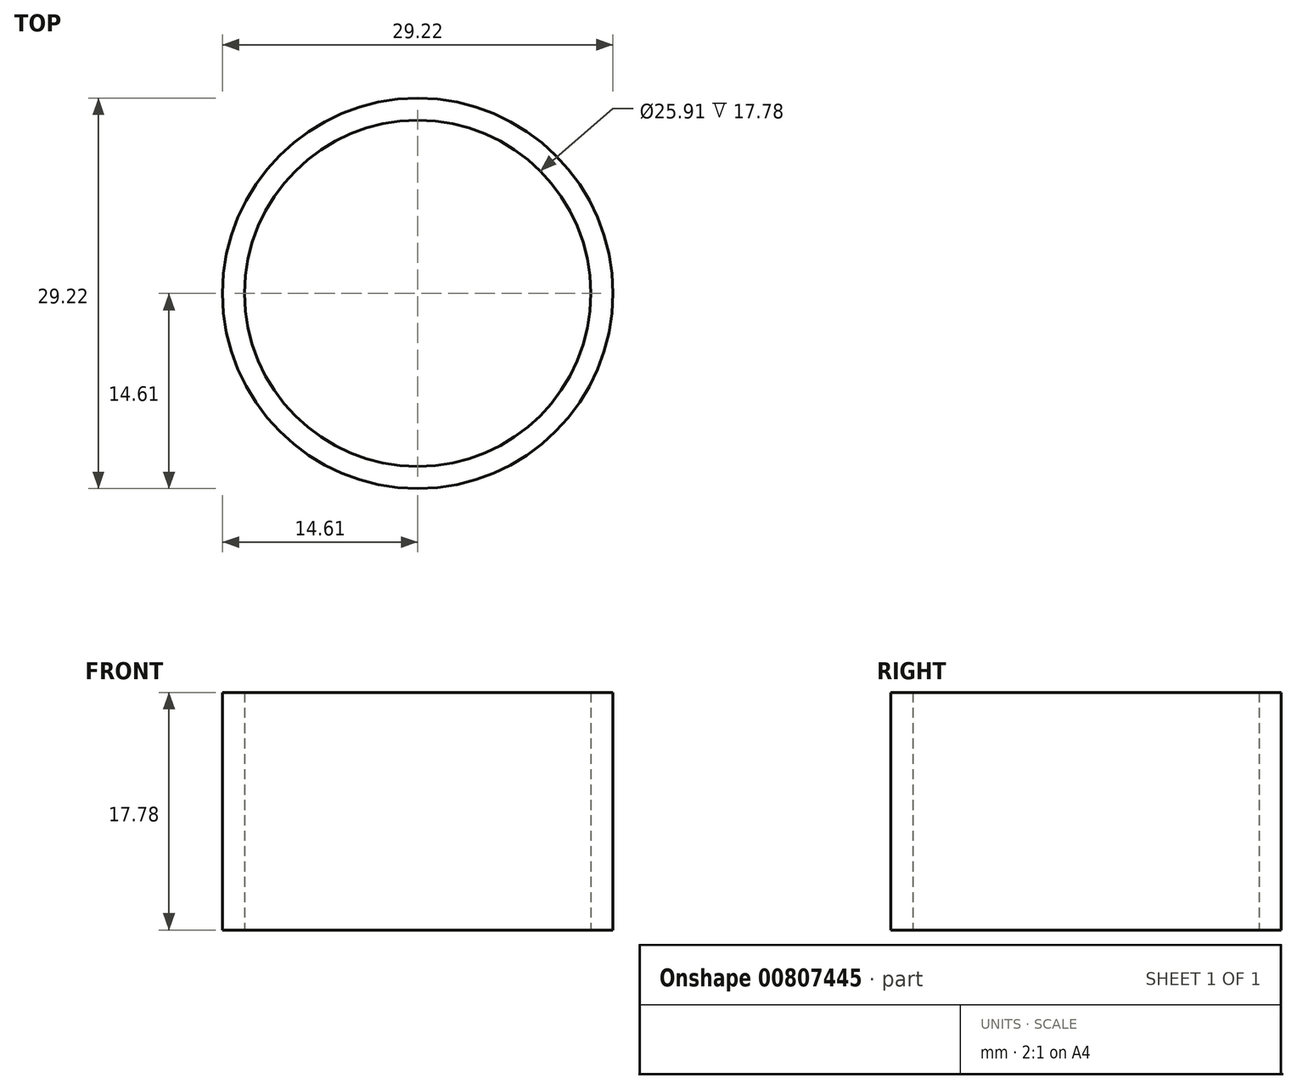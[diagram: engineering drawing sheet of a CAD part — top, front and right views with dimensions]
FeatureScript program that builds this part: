
annotation { "Feature Type Name" : "Feature", "Feature Type Description" : "" }
export const myFeature = defineFeature(function(context is Context, id is Id, definition is map)
    precondition{}
    {
        {
            var Q0;
            Q0=qCreatedBy(makeId("Top.planeOp"),FACE);
            var sketch = newSketch(context, id + "F0", { "sketchPlane" : qUnion([Q0])});
            skCircle(sketch, "E0", {"center": v(0, 0) * mm, "radius": 14.6 * mm});
            skCircle(sketch, "E1", {"center": v(0, 0) * mm, "radius": 12.95 * mm});
            skSolve(sketch);
        }
        {
            var Q0;
            Q0=makeQuery(id+"F0.imprint","IMPRINT",FACE,{"disambiguationData":[TD([[makeQuery(id+"F0.imprint","IMPRINT",EDGE,{"derivedFrom":sQuery(id+"F0.wireOp",EDGE,"E0")}),1.0]])]});
            extrude(context, id + "F1", {"entities" : qUnion([Q0]), "depth" : 17.78 * mm, "offsetDistance" : 25.4 * mm});
        }
    });
